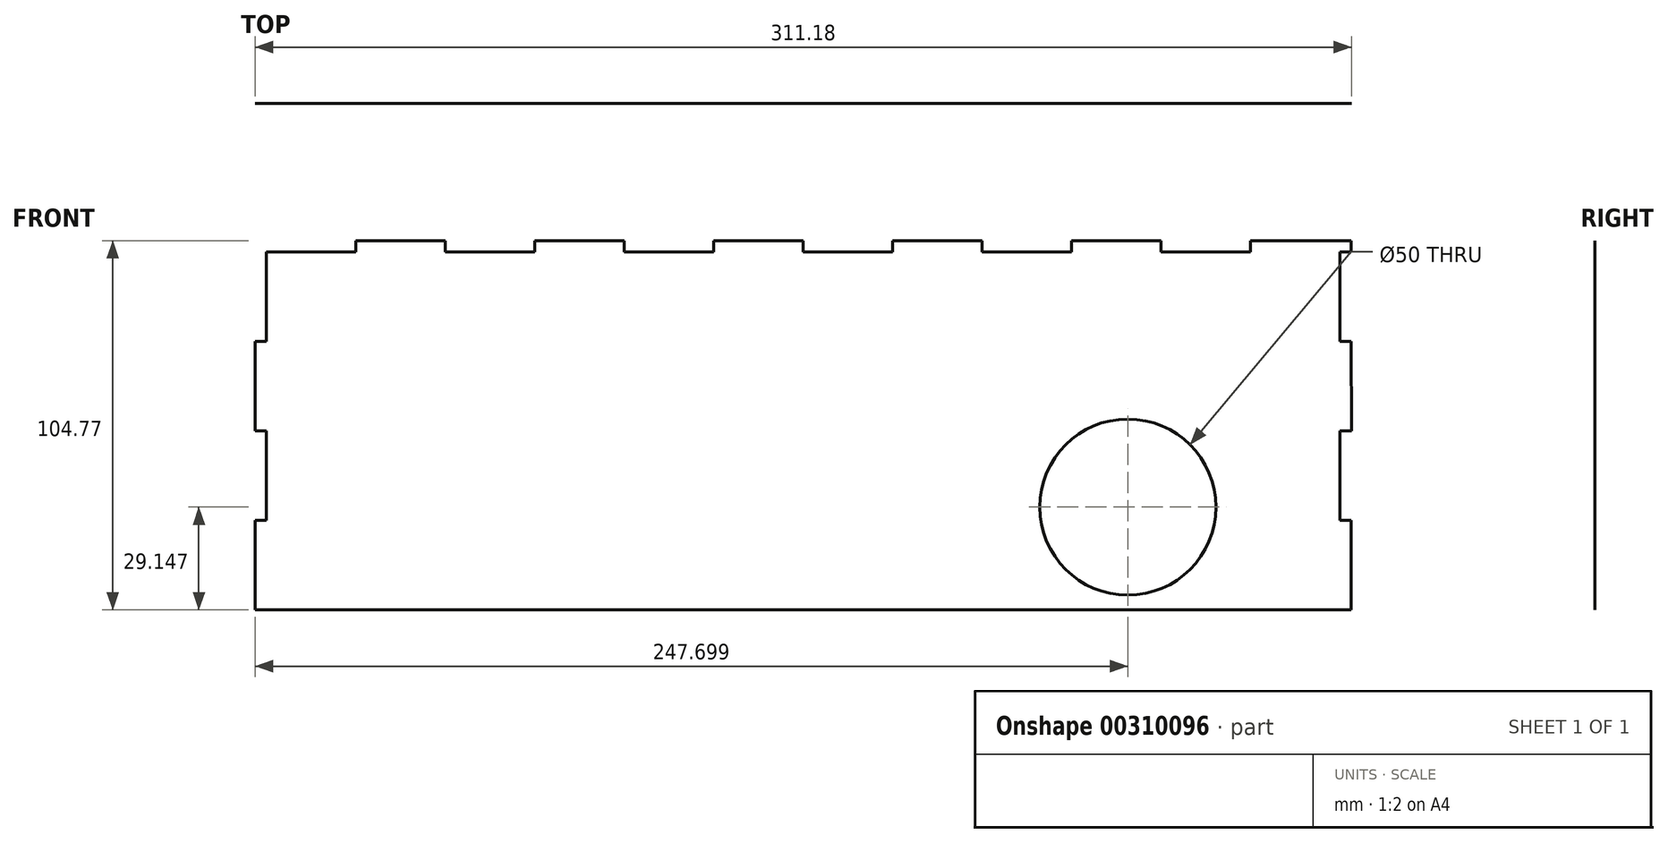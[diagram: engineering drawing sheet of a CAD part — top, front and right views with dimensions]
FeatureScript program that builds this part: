
annotation { "Feature Type Name" : "Feature", "Feature Type Description" : "" }
export const myFeature = defineFeature(function(context is Context, id is Id, definition is map)
    precondition{}
    {
        {
            var Q0;
            Q0=qCreatedBy(makeId("Front.planeOp"),FACE);
            var sketch = newSketch(context, id + "F0", { "sketchPlane" : qUnion([Q0])});
            skLineSegment(sketch, "E0", {"start": v(-178.96, 6.54) * mm, "end": v(-182.14, 6.54) * mm});
            skLineSegment(sketch, "E1", {"start": v(-182.14, 6.54) * mm, "end": v(-182.14, 31.94) * mm});
            skLineSegment(sketch, "E2", {"start": v(-182.14, 31.94) * mm, "end": v(-178.96, 31.94) * mm});
            skLineSegment(sketch, "E3", {"start": v(-178.96, 31.94) * mm, "end": v(-178.96, 57.34) * mm});
            skLineSegment(sketch, "E4", {"start": v(-178.96, 57.34) * mm, "end": v(-182.14, 57.34) * mm});
            skLineSegment(sketch, "E5", {"start": v(-182.14, 57.34) * mm, "end": v(-182.14, 82.74) * mm});
            skLineSegment(sketch, "E6", {"start": v(-182.14, 82.74) * mm, "end": v(-178.96, 82.74) * mm});
            skLineSegment(sketch, "E7", {"start": v(-178.96, 82.74) * mm, "end": v(-178.96, 108.14) * mm});
            skLineSegment(sketch, "E8", {"start": v(-178.96, 108.14) * mm, "end": v(-153.56, 108.14) * mm});
            skLineSegment(sketch, "E9", {"start": v(125.84, 108.14) * mm, "end": v(125.84, 82.74) * mm});
            skLineSegment(sketch, "E10.MirrorCS", {"start": v(-153.56, 111.31) * mm, "end": v(-128.16, 111.31) * mm});
            skLineSegment(sketch, "E11.MirrorCS", {"start": v(-102.76, 111.31) * mm, "end": v(-77.36, 111.31) * mm});
            skLineSegment(sketch, "E12.MirrorCS", {"start": v(-51.96, 111.31) * mm, "end": v(-26.56, 111.31) * mm});
            skLineSegment(sketch, "E13.MirrorCS", {"start": v(-1.16, 111.31) * mm, "end": v(24.24, 111.31) * mm});
            skLineSegment(sketch, "E14.MirrorCS", {"start": v(49.64, 111.31) * mm, "end": v(75.04, 111.31) * mm});
            skLineSegment(sketch, "E15.MirrorCS", {"start": v(125.84, 111.31) * mm, "end": v(100.44, 111.31) * mm});
            skLineSegment(sketch, "E16.MirrorCS", {"start": v(-153.56, 108.14) * mm, "end": v(-153.56, 111.31) * mm});
            skLineSegment(sketch, "E17.MirrorCS", {"start": v(-128.16, 108.14) * mm, "end": v(-128.16, 111.31) * mm});
            skLineSegment(sketch, "E18.MirrorCS", {"start": v(-102.76, 108.14) * mm, "end": v(-102.76, 111.31) * mm});
            skLineSegment(sketch, "E19.MirrorCS", {"start": v(-51.96, 108.14) * mm, "end": v(-51.96, 111.31) * mm});
            skLineSegment(sketch, "E20.MirrorCS", {"start": v(-77.36, 108.14) * mm, "end": v(-77.36, 111.31) * mm});
            skLineSegment(sketch, "E21.MirrorCS", {"start": v(100.44, 111.31) * mm, "end": v(100.44, 108.14) * mm});
            skLineSegment(sketch, "E22.MirrorCS", {"start": v(75.04, 108.14) * mm, "end": v(75.04, 111.31) * mm});
            skLineSegment(sketch, "E23.MirrorCS", {"start": v(49.64, 108.14) * mm, "end": v(49.64, 111.31) * mm});
            skLineSegment(sketch, "E24.MirrorCS", {"start": v(24.24, 108.14) * mm, "end": v(24.24, 111.31) * mm});
            skLineSegment(sketch, "E25.MirrorCS", {"start": v(-26.56, 108.14) * mm, "end": v(-26.56, 111.31) * mm});
            skLineSegment(sketch, "E26.MirrorCS", {"start": v(-1.16, 108.14) * mm, "end": v(-1.16, 111.31) * mm});
            skLineSegment(sketch, "E27.trimOffspring", {"start": v(-128.16, 108.14) * mm, "end": v(-102.76, 108.14) * mm});
            skLineSegment(sketch, "E28.trimOffspring", {"start": v(-77.36, 108.14) * mm, "end": v(-51.96, 108.14) * mm});
            skLineSegment(sketch, "E29.trimOffspring", {"start": v(-26.56, 108.14) * mm, "end": v(-1.16, 108.14) * mm});
            skLineSegment(sketch, "E30.trimOffspring", {"start": v(24.24, 108.14) * mm, "end": v(49.64, 108.14) * mm});
            skLineSegment(sketch, "E31.trimOffspring", {"start": v(75.04, 108.14) * mm, "end": v(100.44, 108.14) * mm});
            skLineSegment(sketch, "E32.MirrorCS", {"start": v(129.04, 57.34) * mm, "end": v(129.01, 82.74) * mm});
            skLineSegment(sketch, "E33.MirrorCS", {"start": v(129.01, 6.54) * mm, "end": v(129.01, 31.94) * mm});
            skLineSegment(sketch, "E34", {"start": v(129.01, 6.54) * mm, "end": v(125.84, 6.54) * mm});
            skLineSegment(sketch, "E35", {"start": v(129.01, 31.94) * mm, "end": v(125.84, 31.94) * mm});
            skLineSegment(sketch, "E36", {"start": v(129.01, 82.74) * mm, "end": v(125.84, 82.74) * mm});
            skLineSegment(sketch, "E37", {"start": v(129.04, 57.34) * mm, "end": v(125.84, 57.34) * mm});
            skLineSegment(sketch, "E38.trimOffspring", {"start": v(125.84, 57.34) * mm, "end": v(125.84, 31.94) * mm});
            skLineSegment(sketch, "E39", {"start": v(-178.96, 6.54) * mm, "end": v(125.84, 6.54) * mm});
            skLineSegment(sketch, "E40", {"start": v(129.01, 108.14) * mm, "end": v(125.84, 108.14) * mm});
            skLineSegment(sketch, "E41", {"start": v(125.84, 111.31) * mm, "end": v(129.01, 111.31) * mm});
            skLineSegment(sketch, "E42", {"start": v(129.01, 111.31) * mm, "end": v(129.01, 108.14) * mm});
            skCircle(sketch, "E43", {"center": v(65.56, 35.69) * mm, "radius": 25 * mm});
            skPoint(sketch, "E43.centerSnap0", {"position": v(1.78, 35.69) * mm});
            skSolve(sketch);
        }
        {
            var Q0;
            Q0=makeQuery(id+"F0.imprint","IMPRINT",FACE,{"disambiguationData":[TD([[makeQuery(id+"F0.imprint","IMPRINT",EDGE,{"derivedFrom":sQuery(id+"F0.wireOp",EDGE,"E0")}),-1.0]])]});
            extrude(context, id + "F1", {"entities" : qUnion([Q0]), "depth" : 1 / 203.2 * mm});
        }
    });
